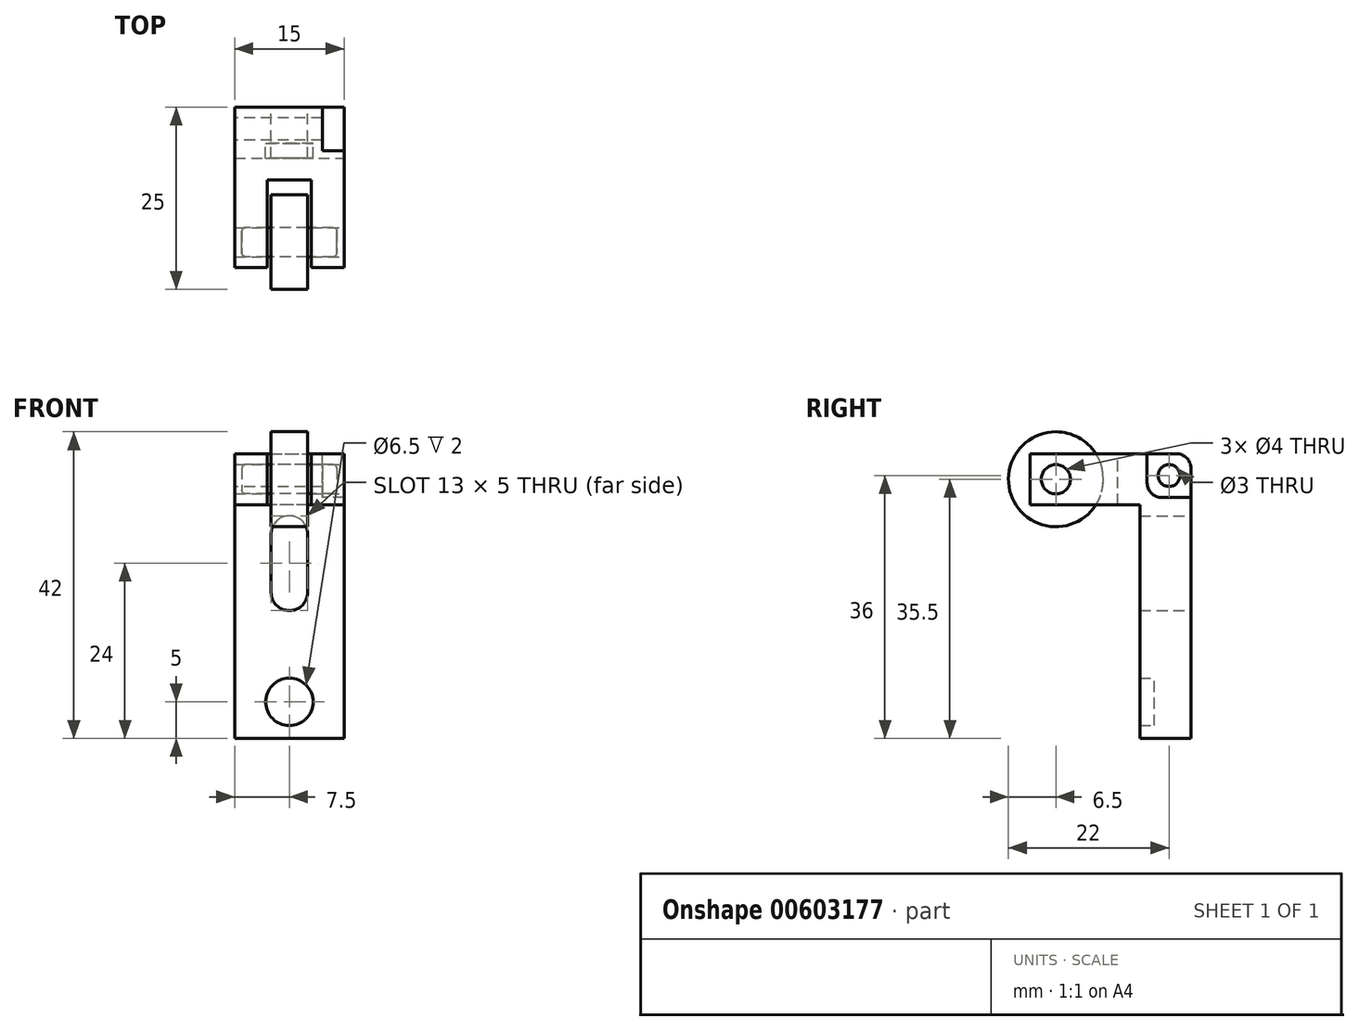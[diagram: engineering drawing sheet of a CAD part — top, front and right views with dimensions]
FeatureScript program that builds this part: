
annotation { "Feature Type Name" : "Feature", "Feature Type Description" : "" }
export const myFeature = defineFeature(function(context is Context, id is Id, definition is map)
    precondition{}
    {
        {
            var Q0;
            Q0=qCreatedBy(makeId("Front.planeOp"),FACE);
            var sketch = newSketch(context, id + "F0", { "sketchPlane" : qUnion([Q0])});
            skLineSegment(sketch, "E0", {"start": v(-7.5, 27) * mm, "end": v(-7.5, -5) * mm});
            skLineSegment(sketch, "E1", {"start": v(-7.5, -5) * mm, "end": v(7.5, -5) * mm});
            skLineSegment(sketch, "E2", {"start": v(7.5, -5) * mm, "end": v(7.5, 27) * mm});
            skLineSegment(sketch, "E3", {"start": v(7.5, 27) * mm, "end": v(-7.5, 27) * mm});
            skLineSegment(sketch, "E4", {"start": v(-7.5, 27) * mm, "end": v(-7.5, 34) * mm});
            skLineSegment(sketch, "E5", {"start": v(-7.5, 34) * mm, "end": v(7.5, 34) * mm});
            skLineSegment(sketch, "E6", {"start": v(7.5, 34) * mm, "end": v(7.5, 27) * mm});
            skPoint(sketch, "E7", {"position": v(0, 0) * mm});
            skLineSegment(sketch, "E8", {"start": v(2.5, 23) * mm, "end": v(2.5, 15) * mm});
            skLineSegment(sketch, "E9", {"start": v(-2.5, 23) * mm, "end": v(-2.5, 15) * mm});
            skArc(sketch, "E10", {"start": v(2.5, 23) * mm, "mid": v(0, 25.5) * mm, "end": v(-2.5, 23) * mm});
            skArc(sketch, "E11", {"start": v(2.5, 15) * mm, "mid": v(0, 12.5) * mm, "end": v(-2.5, 15) * mm});
            skCircle(sketch, "E12", {"center": v(0, 0) * mm, "radius": 3.25 * mm});
            skLineSegment(sketch, "E13", {"start": v(3, 27) * mm, "end": v(3, 34) * mm});
            skLineSegment(sketch, "E14", {"start": v(-3, 27) * mm, "end": v(-3, 34) * mm});
            skSolve(sketch);
        }
        {
            var Q0;
            Q0=makeQuery(id+"F0.imprint","IMPRINT",FACE,{"disambiguationData":[TD([[makeQuery(id+"F0.imprint","IMPRINT",EDGE,{"derivedFrom":sQuery(id+"F0.wireOp",EDGE,"E0")}),1.0]])]});
            extrude(context, id + "F1", {"entities" : qUnion([Q0]), "depth" : 7 * mm, "offsetDistance" : 25 * mm});
        }
        {
            var Q0;
            {var subQ0=sQuery(id+"F0.wireOp",EDGE,"E4");Q0=makeQuery(id+"F0.imprint","IMPRINT",FACE,{"disambiguationData":[TD([[makeQuery(id+"F0.imprint","IMPRINT",EDGE,{"derivedFrom":subQ0}),-1.0]])]});}
            var Q1;
            {var subQ0=sQuery(id+"F0.wireOp",EDGE,"E6");Q1=makeQuery(id+"F0.imprint","IMPRINT",FACE,{"disambiguationData":[TD([[makeQuery(id+"F0.imprint","IMPRINT",EDGE,{"derivedFrom":subQ0}),-1.0]])]});}
            extrude(context, id + "F2", {"entities" : qUnion([Q0, Q1]), "operationType" : NewBodyOperationType.ADD, "depth" : 22 * mm, "offsetDistance" : 25 * mm});
        }
        {
            var Q0;
            Q0=makeQuery(id+"F0.imprint","IMPRINT",FACE,{"disambiguationData":[TD([[makeQuery(id+"F0.imprint","IMPRINT",EDGE,{"derivedFrom":sQuery(id+"F0.wireOp",EDGE,"E12")}),1.0]])]});
            extrude(context, id + "F3", {"entities" : qUnion([Q0]), "operationType" : NewBodyOperationType.ADD, "depth" : 5 * mm, "offsetDistance" : 25 * mm});
        }
        {
            var Q0;
            {var subQ0=sQuery(id+"F0.wireOp",EDGE,"E13");Q0=makeQuery(id+"F0.imprint","IMPRINT",FACE,{"disambiguationData":[TD([[makeQuery(id+"F0.imprint","IMPRINT",EDGE,{"derivedFrom":subQ0}),1.0]])]});}
            extrude(context, id + "F4", {"entities" : qUnion([Q0]), "operationType" : NewBodyOperationType.ADD, "depth" : 10 * mm, "offsetDistance" : 25 * mm});
        }
        {
            var Q0;
            {var subQ0=sQuery(id+"F0.wireOp",EDGE,"E5");Q0=makeQuery(id+"F4.boolean.opBoolean","MERGE",EDGE,{"derivedFrom":[makeQuery(id+"F2.opExtrude","CAP_EDGE",EDGE,{"disambiguationData":[OSD([subQ0]),TDD([makeQuery(id+"F0.imprint","IMPRINT",EDGE,{"disambiguationData":[TD([[makeQuery(id+"F0.imprint","INTERSECT",VERTEX,{"derivedFrom":[sQuery(id+"F0.wireOp",EDGE,"E4"),subQ0]}),-1.0]])],"derivedFrom":subQ0})])],"isStart":true}),makeQuery(id+"F2.opExtrude","CAP_EDGE",EDGE,{"disambiguationData":[OSD([subQ0]),TDD([makeQuery(id+"F0.imprint","IMPRINT",EDGE,{"disambiguationData":[TD([[makeQuery(id+"F0.imprint","INTERSECT",VERTEX,{"derivedFrom":[subQ0,sQuery(id+"F0.wireOp",EDGE,"E6")]}),1.0]])],"derivedFrom":subQ0})])],"isStart":true}),makeQuery(id+"F4.opExtrude","CAP_EDGE",EDGE,{"disambiguationData":[OSD([subQ0])],"isStart":true})]});}
            var Q1;
            {var subQ0=sQuery(id+"F0.wireOp",EDGE,"E3");var subQ4=makeQuery(id+"F1.opExtrude","CAP_EDGE",EDGE,{"disambiguationData":[OSD([subQ0])],"isStart":false});Q1=makeQuery(id+"F4.boolean.opBoolean","MERGE",EDGE,{"derivedFrom":[makeQuery(id+"F2.boolean.opBoolean","SPLIT",EDGE,{"disambiguationData":[topologyDisambiguationEdgeConnected([makeQuery(id+"F2.opExtrude","SWEPT_FACE",FACE,{"disambiguationData":[OSD([subQ0]),TDD([makeQuery(id+"F0.imprint","IMPRINT",EDGE,{"disambiguationData":[TD([[makeQuery(id+"F0.imprint","INTERSECT",VERTEX,{"derivedFrom":[subQ0,sQuery(id+"F0.wireOp",EDGE,"E14")]}),-1.0]])],"derivedFrom":subQ0})])]})])],"derivedFrom":subQ4}),makeQuery(id+"F2.boolean.opBoolean","SPLIT",EDGE,{"disambiguationData":[topologyDisambiguationEdgeConnected([makeQuery(id+"F2.opExtrude","SWEPT_FACE",FACE,{"disambiguationData":[OSD([subQ0]),TDD([makeQuery(id+"F0.imprint","IMPRINT",EDGE,{"disambiguationData":[TD([[makeQuery(id+"F0.imprint","INTERSECT",VERTEX,{"derivedFrom":[subQ0,sQuery(id+"F0.wireOp",EDGE,"E13")]}),1.0]])],"derivedFrom":subQ0})])]})])],"derivedFrom":subQ4}),makeQuery(id+"F2.boolean.opBoolean","SPLIT",EDGE,{"disambiguationData":[topologyDisambiguationEdgeConnected([makeQuery(id+"F1.opExtrude","SWEPT_FACE",FACE,{"disambiguationData":[OSD([subQ0])]})])],"derivedFrom":subQ4})]});}
            fillet(context, id + "F5", {"entities" : qUnion([Q0, Q1]), "radius" : 2 * mm, "tangentPropagation" : true, "allowEdgeOverflow" : false});
        }
        {
            var Q0;
            Q0=makeQuery(id+"F2.boolean.opBoolean","MERGE",FACE,{"derivedFrom":[makeQuery(id+"F1.opExtrude","SWEPT_FACE",FACE,{"disambiguationData":[OSD([sQuery(id+"F0.wireOp",EDGE,"E0")])]}),makeQuery(id+"F2.opExtrude","SWEPT_FACE",FACE,{"disambiguationData":[OSD([sQuery(id+"F0.wireOp",EDGE,"E4")])]})]});
            var sketch = newSketch(context, id + "F6", { "sketchPlane" : qUnion([Q0])});
            skLineSegment(sketch, "E15.0", {"start": v(22, 27) * mm, "end": v(22, 34) * mm});
            skPoint(sketch, "E16", {"position": v(18.5, 30.5) * mm});
            skLineSegment(sketch, "E17", {"start": v(4, 28) * mm, "end": v(0, 28) * mm});
            skLineSegment(sketch, "E18", {"start": v(6, 30) * mm, "end": v(6, 34) * mm});
            skLineSegment(sketch, "E19", {"start": v(6, 34) * mm, "end": v(0, 34) * mm});
            skLineSegment(sketch, "E20", {"start": v(0, 34) * mm, "end": v(0, 28) * mm});
            skPoint(sketch, "E21.visualSharp", {"position": v(6, 28) * mm});
            skArc(sketch, "E21.filletArc", {"start": v(4, 28) * mm, "mid": v(5.41, 28.59) * mm, "end": v(6, 30) * mm});
            skCircle(sketch, "E22", {"center": v(3, 31) * mm, "radius": 1.5 * mm});
            skCircle(sketch, "E23", {"center": v(18.5, 30.5) * mm, "radius": 6.5 * mm});
            skCircle(sketch, "E24", {"center": v(18.5, 30.5) * mm, "radius": 2 * mm});
            skLineSegment(sketch, "E25", {"start": v(-27.02, 67.3) * mm, "end": v(54.6, 67.3) * mm, "construction": true});
            skSolve(sketch);
        }
        {
            var Q0;
            Q0=sQuery(id+"F6.wireOp",VERTEX,"E16");
            var Q1;
            Q1=makeQuery(id+"F1.opExtrude","SWEPT_BODY",BODY,{"disambiguationData":[OSD([sQuery(id+"F0.wireOp",EDGE,"E0"),sQuery(id+"F0.wireOp",EDGE,"E1"),sQuery(id+"F0.wireOp",EDGE,"E2"),sQuery(id+"F0.wireOp",EDGE,"E3"),sQuery(id+"F0.wireOp",EDGE,"E8"),sQuery(id+"F0.wireOp",EDGE,"E9"),sQuery(id+"F0.wireOp",EDGE,"E10"),sQuery(id+"F0.wireOp",EDGE,"E11"),sQuery(id+"F0.wireOp",EDGE,"E12")])]});
            hole(context, id + "F7", {"style" : HoleStyle.SIMPLE, "endStyle" : HoleEndStyle.BLIND, "holeDiameter" : 4 * mm, "majorDiameter" : 5 * mm, "holeDepth" : 20 * mm, "isTappedThrough" : true, "tappedDepth" : 12 * mm, "tapClearance" : 3, "locations" : qUnion([Q0]), "scope" : qUnion([Q1])});
        }
        {
            var Q0;
            Q0=makeQuery(id+"F6.imprint","IMPRINT",FACE,{"disambiguationData":[TD([[makeQuery(id+"F6.imprint","IMPRINT",EDGE,{"derivedFrom":sQuery(id+"F6.wireOp",EDGE,"E22")}),1.0]])]});
            extrude(context, id + "F8", {"entities" : qUnion([Q0]), "operationType" : NewBodyOperationType.REMOVE, "oppositeDirection" : true, "depth" : 25 * mm, "offsetDistance" : 25 * mm});
        }
        {
            var Q0;
            {var subQ7=sQuery(id+"F6.wireOp",EDGE,"E17");Q0=makeQuery(id+"F6.imprint","IMPRINT",FACE,{"disambiguationData":[TD([[makeQuery(id+"F6.imprint","IMPRINT",EDGE,{"derivedFrom":subQ7}),-1.0]])]});}
            extrude(context, id + "F9", {"entities" : qUnion([Q0]), "operationType" : NewBodyOperationType.REMOVE, "oppositeDirection" : true, "depth" : 15 * mm, "offsetDistance" : 25 * mm, "hasSecondDirection" : true, "secondDirectionOppositeDirection" : true, "secondDirectionDepth" : 12 * mm});
        }
        {
            var Q0;
            {var subQ0=sQuery(id+"F6.wireOp",EDGE,"E15.0");Q0=makeQuery(id+"F6.imprint","IMPRINT",FACE,{"disambiguationData":[TD([[makeQuery(id+"F6.imprint","IMPRINT",EDGE,{"derivedFrom":subQ0}),-1.0]])]});}
            var Q1;
            {var subQ0=sQuery(id+"F6.wireOp",EDGE,"E15.0");Q1=makeQuery(id+"F6.imprint","IMPRINT",FACE,{"disambiguationData":[TD([[makeQuery(id+"F6.imprint","IMPRINT",EDGE,{"derivedFrom":subQ0}),1.0]])]});}
            extrude(context, id + "F10", {"entities" : qUnion([Q0, Q1]), "oppositeDirection" : true, "depth" : 10 * mm, "offsetDistance" : 25 * mm, "hasSecondDirection" : true, "secondDirectionOppositeDirection" : true, "secondDirectionDepth" : 5 * mm});
        }
        {
            var Q0;
            Q0=makeQuery(id+"F6.imprint","IMPRINT",FACE,{"disambiguationData":[TD([[makeQuery(id+"F6.imprint","IMPRINT",EDGE,{"derivedFrom":sQuery(id+"F6.wireOp",EDGE,"E24")}),1.0]])]});
            extrude(context, id + "F11", {"entities" : qUnion([Q0]), "oppositeDirection" : true, "depth" : 14 * mm, "offsetDistance" : 25 * mm, "hasSecondDirection" : true, "secondDirectionOppositeDirection" : true, "secondDirectionDepth" : 1 * mm});
        }
        {
            var Q0;
            Q0=makeQuery(id+"F11.opExtrude","CAP_EDGE",EDGE,{"disambiguationData":[OSD([sQuery(id+"F6.wireOp",EDGE,"E24")])],"isStart":true});
            fillet(context, id + "F12", {"entities" : qUnion([Q0]), "radius" : .5 * mm, "tangentPropagation" : true, "allowEdgeOverflow" : false});
        }
        {
            var Q0;
            Q0=makeQuery(id+"F11.opExtrude","CAP_EDGE",EDGE,{"disambiguationData":[OSD([sQuery(id+"F6.wireOp",EDGE,"E24")])],"isStart":false});
            fillet(context, id + "F13", {"entities" : qUnion([Q0]), "radius" : .5 * mm, "tangentPropagation" : true, "allowEdgeOverflow" : false});
        }
    });
